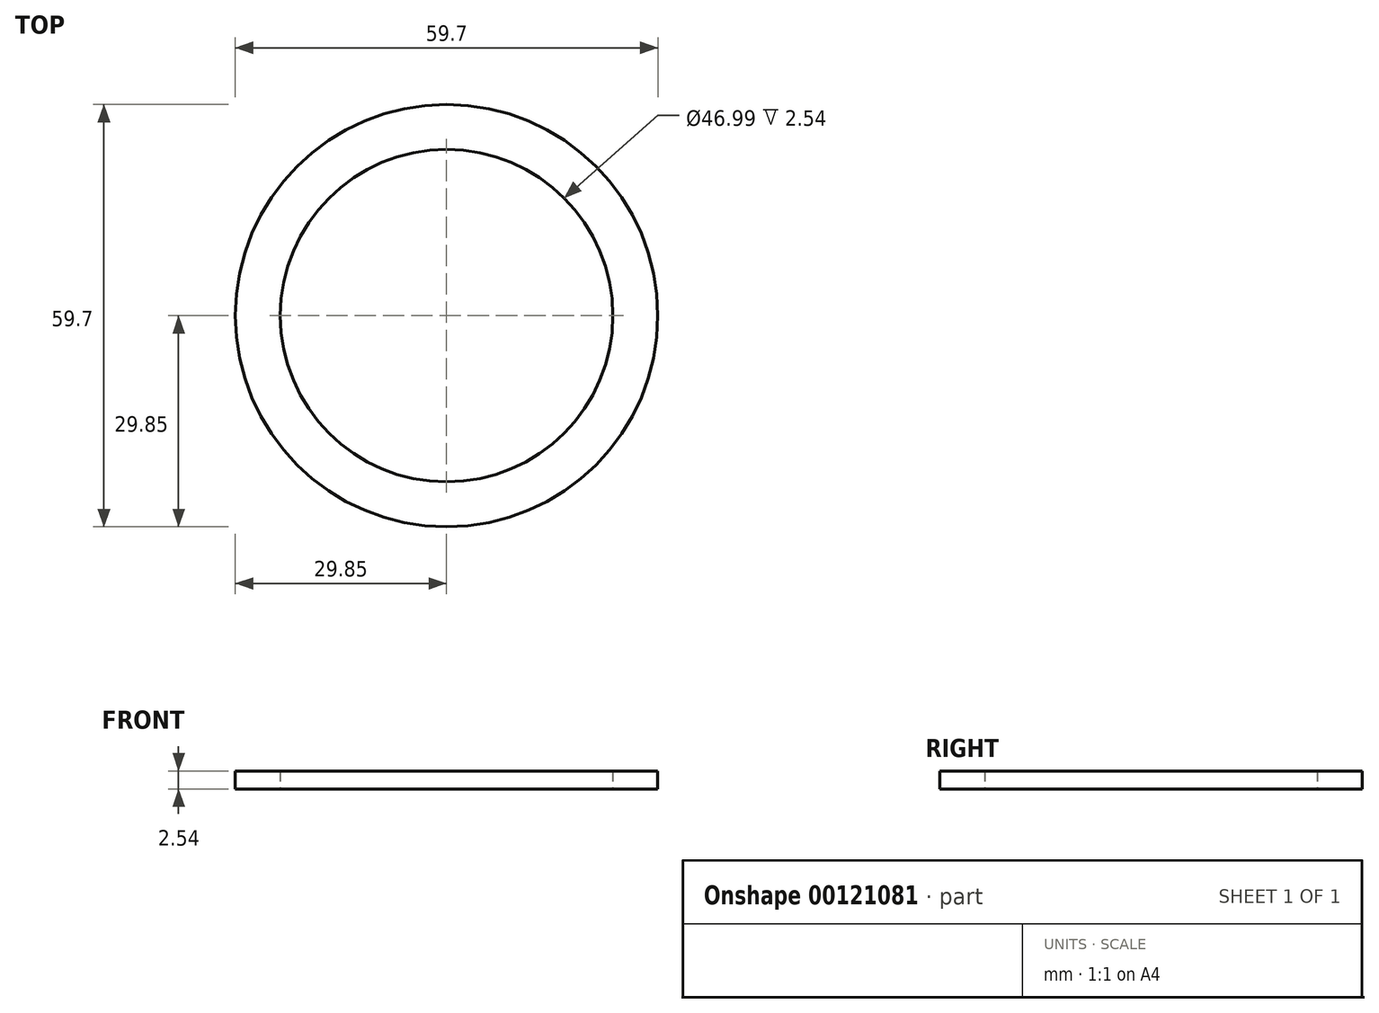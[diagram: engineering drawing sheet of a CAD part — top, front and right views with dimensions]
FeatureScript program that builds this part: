
annotation { "Feature Type Name" : "Feature", "Feature Type Description" : "" }
export const myFeature = defineFeature(function(context is Context, id is Id, definition is map)
    precondition{}
    {
        {
            var Q0;
            Q0=qCreatedBy(makeId("Top.planeOp"),FACE);
            var sketch = newSketch(context, id + "F0", { "sketchPlane" : qUnion([Q0])});
            skCircle(sketch, "E0", {"center": v(0, 0) * mm, "radius": 29.85 * mm});
            skCircle(sketch, "E1", {"center": v(0, 0) * mm, "radius": 23.5 * mm});
            skSolve(sketch);
        }
        {
            var Q0;
            Q0 = qSketchRegion(id + "F0", true);
            extrude(context, id + "F1", {"entities" : qUnion([Q0]), "depth" : 2.54 * mm});
        }
    });
